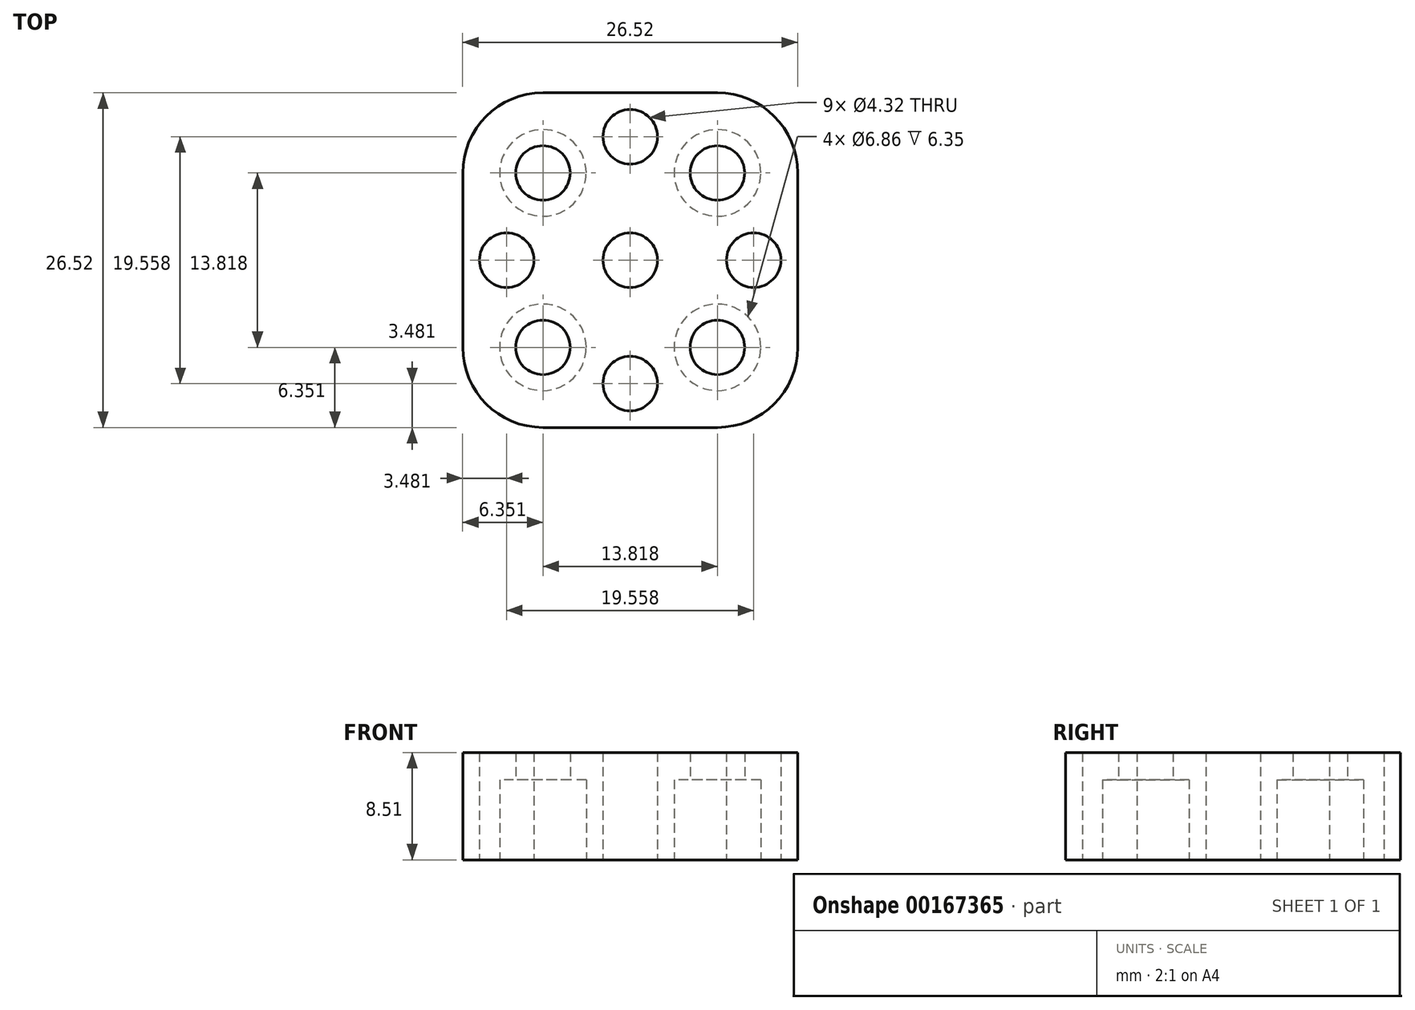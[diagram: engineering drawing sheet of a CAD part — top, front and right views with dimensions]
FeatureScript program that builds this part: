
annotation { "Feature Type Name" : "Feature", "Feature Type Description" : "" }
export const myFeature = defineFeature(function(context is Context, id is Id, definition is map)
    precondition{}
    {
        {
            var Q0;
            Q0=qCreatedBy(makeId("Top.planeOp"),FACE);
            var sketch = newSketch(context, id + "F0", { "sketchPlane" : qUnion([Q0])});
            skLineSegment(sketch, "E0.bottom", {"start": v(6.9, 13.26) * mm, "end": v(-6.9, 13.26) * mm});
            skLineSegment(sketch, "E0.top", {"start": v(6.9, -13.26) * mm, "end": v(-6.9, -13.26) * mm});
            skLineSegment(sketch, "E0.left", {"start": v(13.26, 6.9) * mm, "end": v(13.26, -6.9) * mm});
            skLineSegment(sketch, "E0.right", {"start": v(-13.26, 6.9) * mm, "end": v(-13.26, -6.9) * mm});
            skPoint(sketch, "E0.middle", {"position": v(0, 0) * mm});
            skCircle(sketch, "E1", {"center": v(0, 0) * mm, "radius": 2.16 * mm});
            skCircle(sketch, "E2", {"center": v(-6.9, 6.9) * mm, "radius": 2.16 * mm});
            skCircle(sketch, "E3", {"center": v(-9.78, 0) * mm, "radius": 2.16 * mm});
            skCircle(sketch, "E4", {"center": v(-6.9, -6.9) * mm, "radius": 2.16 * mm});
            skCircle(sketch, "E5", {"center": v(6.9, -6.9) * mm, "radius": 2.16 * mm});
            skCircle(sketch, "E6", {"center": v(9.78, 0) * mm, "radius": 2.16 * mm});
            skCircle(sketch, "E7", {"center": v(6.9, 6.9) * mm, "radius": 2.16 * mm});
            skLineSegment(sketch, "E8", {"start": v(-6.9, 6.9) * mm, "end": v(6.9, 6.9) * mm, "construction": true});
            skLineSegment(sketch, "E9", {"start": v(6.9, -6.9) * mm, "end": v(-6.9, -6.9) * mm, "construction": true});
            skLineSegment(sketch, "E10", {"start": v(-6.9, -6.9) * mm, "end": v(-6.9, 6.9) * mm, "construction": true});
            skLineSegment(sketch, "E11", {"start": v(6.9, 6.9) * mm, "end": v(6.9, -6.9) * mm, "construction": true});
            skLineSegment(sketch, "E12", {"start": v(-6.9, -6.9) * mm, "end": v(6.9, 6.9) * mm, "construction": true});
            skLineSegment(sketch, "E13", {"start": v(0, 13.26) * mm, "end": v(0, -13.26) * mm});
            skCircle(sketch, "E14", {"center": v(0, 9.78) * mm, "radius": 2.16 * mm});
            skCircle(sketch, "E15", {"center": v(0, -9.78) * mm, "radius": 2.16 * mm});
            skPoint(sketch, "E16.visualSharp", {"position": v(-13.26, 13.26) * mm});
            skArc(sketch, "E16.filletArc", {"start": v(-6.9, 13.26) * mm, "mid": v(-11.4, 11.4) * mm, "end": v(-13.26, 6.9) * mm});
            skPoint(sketch, "E17.visualSharp", {"position": v(13.26, 13.26) * mm});
            skArc(sketch, "E17.filletArc", {"start": v(13.26, 6.9) * mm, "mid": v(11.4, 11.4) * mm, "end": v(6.9, 13.26) * mm});
            skPoint(sketch, "E18.visualSharp", {"position": v(13.26, -13.26) * mm});
            skArc(sketch, "E18.filletArc", {"start": v(6.9, -13.26) * mm, "mid": v(11.4, -11.4) * mm, "end": v(13.26, -6.9) * mm});
            skPoint(sketch, "E19.visualSharp", {"position": v(-13.26, -13.26) * mm});
            skArc(sketch, "E19.filletArc", {"start": v(-13.26, -6.9) * mm, "mid": v(-11.4, -11.4) * mm, "end": v(-6.9, -13.26) * mm});
            skCircle(sketch, "E20", {"center": v(-6.9, 6.9) * mm, "radius": 3.43 * mm});
            skCircle(sketch, "E21", {"center": v(6.9, 6.9) * mm, "radius": 3.43 * mm});
            skCircle(sketch, "E22", {"center": v(6.9, -6.9) * mm, "radius": 3.43 * mm});
            skCircle(sketch, "E23", {"center": v(-6.9, -6.9) * mm, "radius": 3.43 * mm});
            skLineSegment(sketch, "E24", {"start": v(-13.26, 0) * mm, "end": v(13.26, 0) * mm, "construction": true});
            skSolve(sketch);
        }
        {
            var Q0;
            Q0=makeQuery(id+"F0.imprint","IMPRINT",FACE,{"disambiguationData":[TD([[makeQuery(id+"F0.imprint","IMPRINT",EDGE,{"derivedFrom":sQuery(id+"F0.wireOp",EDGE,"E0.right")}),1.0]])]});
            var Q1;
            Q1=makeQuery(id+"F0.imprint","IMPRINT",FACE,{"disambiguationData":[TD([[makeQuery(id+"F0.imprint","IMPRINT",EDGE,{"derivedFrom":sQuery(id+"F0.wireOp",EDGE,"E0.left")}),-1.0]])]});
            var Q2;
            Q2=makeQuery(id+"F0.imprint","IMPRINT",FACE,{"disambiguationData":[TD([[makeQuery(id+"F0.imprint","IMPRINT",EDGE,{"derivedFrom":sQuery(id+"F0.wireOp",EDGE,"E2")}),-1.0]])]});
            var Q3;
            Q3=makeQuery(id+"F0.imprint","IMPRINT",FACE,{"disambiguationData":[TD([[makeQuery(id+"F0.imprint","IMPRINT",EDGE,{"derivedFrom":sQuery(id+"F0.wireOp",EDGE,"E4")}),-1.0]])]});
            var Q4;
            Q4=makeQuery(id+"F0.imprint","IMPRINT",FACE,{"disambiguationData":[TD([[makeQuery(id+"F0.imprint","IMPRINT",EDGE,{"derivedFrom":sQuery(id+"F0.wireOp",EDGE,"E5")}),-1.0]])]});
            var Q5;
            Q5=makeQuery(id+"F0.imprint","IMPRINT",FACE,{"disambiguationData":[TD([[makeQuery(id+"F0.imprint","IMPRINT",EDGE,{"derivedFrom":sQuery(id+"F0.wireOp",EDGE,"E7")}),-1.0]])]});
            extrude(context, id + "F1", {"entities" : qUnion([Q0, Q1, Q2, Q3, Q4, Q5]), "depth" : 8.5 * mm});
        }
        {
            var Q0;
            Q0=makeQuery(id+"F0.imprint","IMPRINT",FACE,{"disambiguationData":[TD([[makeQuery(id+"F0.imprint","IMPRINT",EDGE,{"derivedFrom":sQuery(id+"F0.wireOp",EDGE,"E4")}),-1.0]])]});
            var Q1;
            Q1=makeQuery(id+"F0.imprint","IMPRINT",FACE,{"disambiguationData":[TD([[makeQuery(id+"F0.imprint","IMPRINT",EDGE,{"derivedFrom":sQuery(id+"F0.wireOp",EDGE,"E5")}),-1.0]])]});
            var Q2;
            Q2=makeQuery(id+"F0.imprint","IMPRINT",FACE,{"disambiguationData":[TD([[makeQuery(id+"F0.imprint","IMPRINT",EDGE,{"derivedFrom":sQuery(id+"F0.wireOp",EDGE,"E7")}),-1.0]])]});
            var Q3;
            Q3=makeQuery(id+"F0.imprint","IMPRINT",FACE,{"disambiguationData":[TD([[makeQuery(id+"F0.imprint","IMPRINT",EDGE,{"derivedFrom":sQuery(id+"F0.wireOp",EDGE,"E2")}),-1.0]])]});
            extrude(context, id + "F2", {"entities" : qUnion([Q0, Q1, Q2, Q3]), "operationType" : NewBodyOperationType.REMOVE, "depth" : 6.35 * mm});
        }
    });
